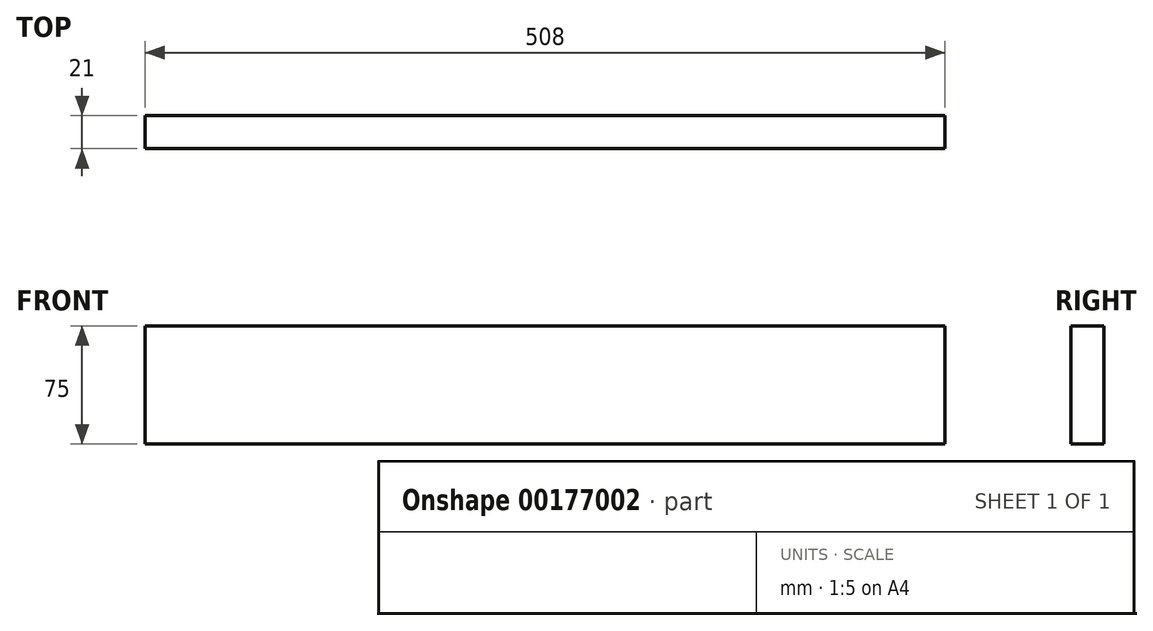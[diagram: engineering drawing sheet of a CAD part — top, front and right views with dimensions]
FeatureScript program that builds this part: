
annotation { "Feature Type Name" : "Feature", "Feature Type Description" : "" }
export const myFeature = defineFeature(function(context is Context, id is Id, definition is map)
    precondition{}
    {
        {
            var Q0;
            Q0=qCreatedBy(makeId("Front.planeOp"),FACE);
            var sketch = newSketch(context, id + "F0", { "sketchPlane" : qUnion([Q0])});
            skLineSegment(sketch, "E0.bottom", {"start": v(0, 0) * mm, "end": v(508, 0) * mm});
            skLineSegment(sketch, "E0.top", {"start": v(0, 75) * mm, "end": v(508, 75) * mm});
            skLineSegment(sketch, "E0.left", {"start": v(0, 0) * mm, "end": v(0, 75) * mm});
            skLineSegment(sketch, "E0.right", {"start": v(508, 0) * mm, "end": v(508, 75) * mm});
            skSolve(sketch);
        }
        {
            var Q0;
            Q0=makeQuery(id+"F0.imprint","IMPRINT",FACE,{"disambiguationData":[TD([[makeQuery(id+"F0.imprint","IMPRINT",EDGE,{"derivedFrom":sQuery(id+"F0.wireOp",EDGE,"E0.bottom")}),1.0]])]});
            extrude(context, id + "F1", {"entities" : qUnion([Q0]), "depth" : 21 * mm});
        }
    });
